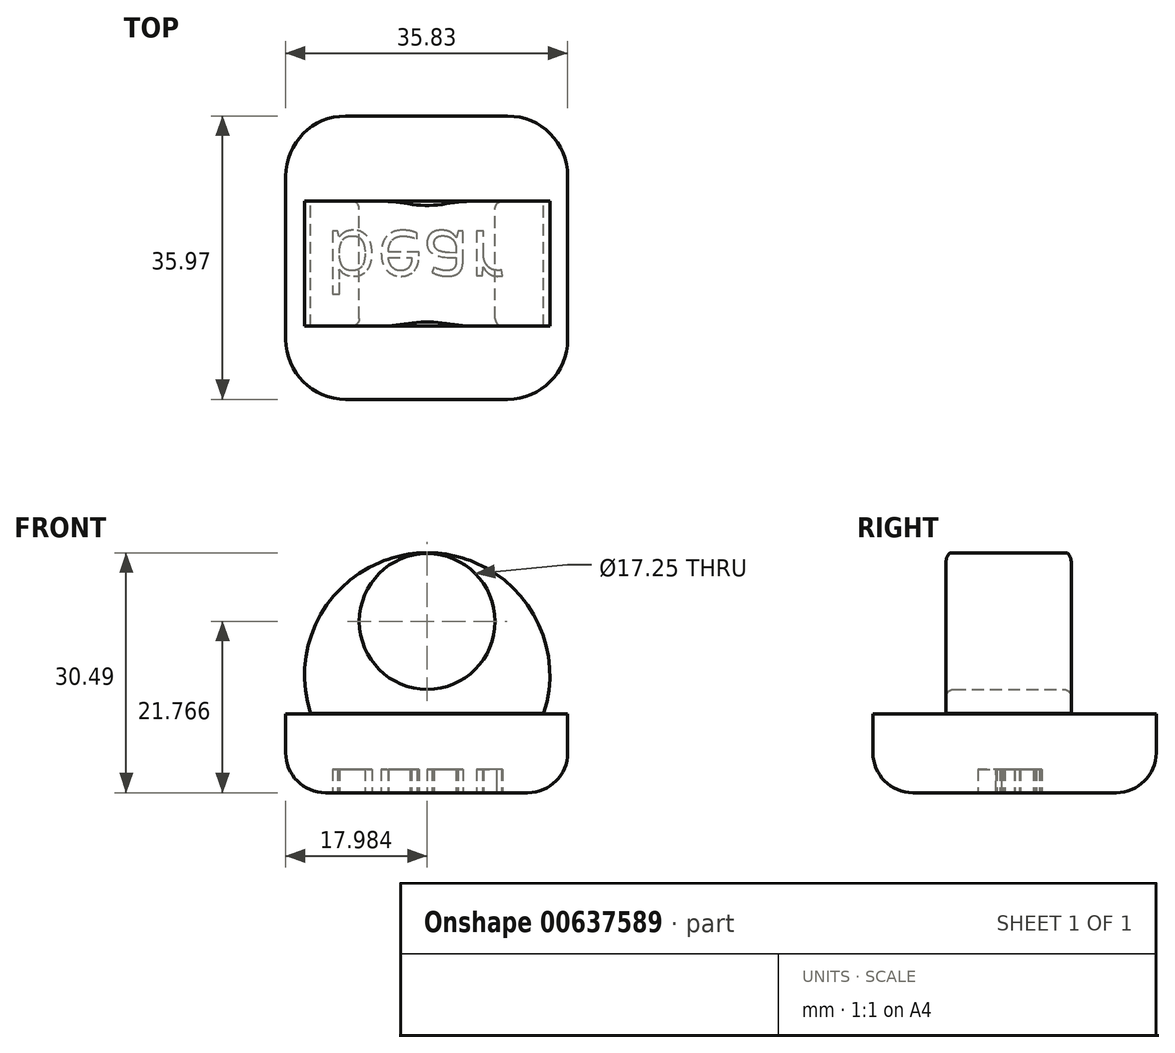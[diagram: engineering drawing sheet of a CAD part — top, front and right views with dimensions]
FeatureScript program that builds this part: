
annotation { "Feature Type Name" : "Feature", "Feature Type Description" : "" }
export const myFeature = defineFeature(function(context is Context, id is Id, definition is map)
    precondition{}
    {
        {
            var Q0;
            Q0=qCreatedBy(makeId("Top.planeOp"),FACE);
            var sketch = newSketch(context, id + "F0", { "sketchPlane" : qUnion([Q0])});
            skLineSegment(sketch, "E0", {"start": v(-35.83, -25.18) * mm, "end": v(0, -25.18) * mm});
            skLineSegment(sketch, "E1", {"start": v(0, -25.18) * mm, "end": v(0, 10.8) * mm});
            skLineSegment(sketch, "E2", {"start": v(0, 10.8) * mm, "end": v(-35.83, 10.8) * mm});
            skLineSegment(sketch, "E3", {"start": v(-35.83, 10.8) * mm, "end": v(-35.83, -25.18) * mm});
            skSolve(sketch);
        }
        {
            var Q0;
            Q0 = qSketchRegion(id + "F0", true);
            extrude(context, id + "F1", {"entities" : qUnion([Q0]), "depth" : 10 * mm, "offsetDistance" : 25.4 * mm});
        }
        {
            var Q0;
            Q0=qCreatedBy(makeId("Front.planeOp"),FACE);
            var sketch = newSketch(context, id + "F2", { "sketchPlane" : qUnion([Q0])});
            skLineSegment(sketch, "E4", {"start": v(-32.65, 10.06) * mm, "end": v(-29.6, 10.06) * mm});
            skLineSegment(sketch, "E5", {"start": v(-3.05, 10.06) * mm, "end": v(-6.1, 10.06) * mm});
            skPoint(sketch, "E6.orphan", {"position": v(-35.7, 10.06) * mm});
            skPoint(sketch, "E7.orphan", {"position": v(0, 10.06) * mm});
            skCircle(sketch, "E8", {"center": v(-17.85, 21.77) * mm, "radius": 8.63 * mm});
            skArc(sketch, "E9", {"start": v(-3.05, 10.06) * mm, "mid": v(-17.85, 30.5) * mm, "end": v(-32.65, 10.06) * mm});
            skLineSegment(sketch, "E10", {"start": v(-29.6, 10.06) * mm, "end": v(-6.1, 10.06) * mm});
            skSolve(sketch);
        }
        {
            var Q0;
            Q0=makeQuery(id+"F1.opExtrude","SWEPT_EDGE",EDGE,{"disambiguationData":[OSD([sQuery(id+"F0.wireOp",EDGE,"E0"),sQuery(id+"F0.wireOp",EDGE,"E3")])]});
            var Q1;
            Q1=makeQuery(id+"F1.opExtrude","SWEPT_EDGE",EDGE,{"disambiguationData":[OSD([sQuery(id+"F0.wireOp",EDGE,"E2"),sQuery(id+"F0.wireOp",EDGE,"E3")])]});
            var Q2;
            Q2=makeQuery(id+"F1.opExtrude","SWEPT_EDGE",EDGE,{"disambiguationData":[OSD([sQuery(id+"F0.wireOp",EDGE,"E1"),sQuery(id+"F0.wireOp",EDGE,"E2")])]});
            var Q3;
            Q3=makeQuery(id+"F1.opExtrude","SWEPT_EDGE",EDGE,{"disambiguationData":[OSD([sQuery(id+"F0.wireOp",EDGE,"E0"),sQuery(id+"F0.wireOp",EDGE,"E1")])]});
            fillet(context, id + "F3", {"entities" : qUnion([Q0, Q1, Q2, Q3]), "radius" : 7.62 * mm, "tangentPropagation" : true, "allowEdgeOverflow" : false});
        }
        {
            var Q0;
            Q0=makeQuery(id+"F1.opExtrude","CAP_EDGE",EDGE,{"disambiguationData":[OSD([sQuery(id+"F0.wireOp",EDGE,"E0")])],"isStart":true});
            var Q1;
            Q1=makeQuery(id+"F1.opExtrude","CAP_EDGE",EDGE,{"disambiguationData":[OSD([sQuery(id+"F0.wireOp",EDGE,"E3")])],"isStart":true});
            var Q2;
            {var subQ0=sQuery(id+"F0.wireOp",EDGE,"E3");var subQ1=sQuery(id+"F0.wireOp",EDGE,"E0");Q2=makeQuery(id+"F3.opFillet","BLEND_EDGE",EDGE,{"blendedFrom":[makeQuery(id+"F1.opExtrude","SWEPT_EDGE",EDGE,{"disambiguationData":[OSD([subQ1,subQ0])]}),makeQuery(id+"F1.opExtrude","CAP_FACE",FACE,{"disambiguationData":[OSD([subQ1,sQuery(id+"F0.wireOp",EDGE,"E1"),sQuery(id+"F0.wireOp",EDGE,"E2"),subQ0])],"isStart":true})],"blendedInto":[makeQuery(id+"F1.opExtrude","CAP_FACE",FACE,{"disambiguationData":[OSD([subQ1,sQuery(id+"F0.wireOp",EDGE,"E1"),sQuery(id+"F0.wireOp",EDGE,"E2"),subQ0])],"isStart":true})]});}
            var Q3;
            {var subQ0=sQuery(id+"F0.wireOp",EDGE,"E1");var subQ1=sQuery(id+"F0.wireOp",EDGE,"E0");Q3=makeQuery(id+"F3.opFillet","BLEND_EDGE",EDGE,{"blendedFrom":[makeQuery(id+"F1.opExtrude","SWEPT_EDGE",EDGE,{"disambiguationData":[OSD([subQ1,subQ0])]}),makeQuery(id+"F1.opExtrude","CAP_FACE",FACE,{"disambiguationData":[OSD([subQ1,subQ0,sQuery(id+"F0.wireOp",EDGE,"E2"),sQuery(id+"F0.wireOp",EDGE,"E3")])],"isStart":true})],"blendedInto":[makeQuery(id+"F1.opExtrude","CAP_FACE",FACE,{"disambiguationData":[OSD([subQ1,subQ0,sQuery(id+"F0.wireOp",EDGE,"E2"),sQuery(id+"F0.wireOp",EDGE,"E3")])],"isStart":true})]});}
            var Q4;
            Q4=makeQuery(id+"F1.opExtrude","CAP_EDGE",EDGE,{"disambiguationData":[OSD([sQuery(id+"F0.wireOp",EDGE,"E1")])],"isStart":true});
            var Q5;
            {var subQ0=sQuery(id+"F0.wireOp",EDGE,"E2");var subQ1=sQuery(id+"F0.wireOp",EDGE,"E1");Q5=makeQuery(id+"F3.opFillet","BLEND_EDGE",EDGE,{"blendedFrom":[makeQuery(id+"F1.opExtrude","SWEPT_EDGE",EDGE,{"disambiguationData":[OSD([subQ1,subQ0])]}),makeQuery(id+"F1.opExtrude","CAP_FACE",FACE,{"disambiguationData":[OSD([sQuery(id+"F0.wireOp",EDGE,"E0"),subQ1,subQ0,sQuery(id+"F0.wireOp",EDGE,"E3")])],"isStart":true})],"blendedInto":[makeQuery(id+"F1.opExtrude","CAP_FACE",FACE,{"disambiguationData":[OSD([sQuery(id+"F0.wireOp",EDGE,"E0"),subQ1,subQ0,sQuery(id+"F0.wireOp",EDGE,"E3")])],"isStart":true})]});}
            var Q6;
            Q6=makeQuery(id+"F1.opExtrude","CAP_EDGE",EDGE,{"disambiguationData":[OSD([sQuery(id+"F0.wireOp",EDGE,"E2")])],"isStart":true});
            var Q7;
            {var subQ0=sQuery(id+"F0.wireOp",EDGE,"E3");var subQ1=sQuery(id+"F0.wireOp",EDGE,"E2");Q7=makeQuery(id+"F3.opFillet","BLEND_EDGE",EDGE,{"blendedFrom":[makeQuery(id+"F1.opExtrude","SWEPT_EDGE",EDGE,{"disambiguationData":[OSD([subQ1,subQ0])]}),makeQuery(id+"F1.opExtrude","CAP_FACE",FACE,{"disambiguationData":[OSD([sQuery(id+"F0.wireOp",EDGE,"E0"),sQuery(id+"F0.wireOp",EDGE,"E1"),subQ1,subQ0])],"isStart":true})],"blendedInto":[makeQuery(id+"F1.opExtrude","CAP_FACE",FACE,{"disambiguationData":[OSD([sQuery(id+"F0.wireOp",EDGE,"E0"),sQuery(id+"F0.wireOp",EDGE,"E1"),subQ1,subQ0])],"isStart":true})]});}
            fillet(context, id + "F4", {"entities" : qUnion([Q0, Q1, Q2, Q3, Q4, Q5, Q6, Q7]), "radius" : 5.08 * mm, "tangentPropagation" : true, "allowEdgeOverflow" : false});
        }
        {
            var Q0;
            Q0=makeQuery(id+"F1.opExtrude","CAP_FACE",FACE,{"disambiguationData":[OSD([sQuery(id+"F0.wireOp",EDGE,"E0"),sQuery(id+"F0.wireOp",EDGE,"E1"),sQuery(id+"F0.wireOp",EDGE,"E2"),sQuery(id+"F0.wireOp",EDGE,"E3")])],"isStart":true});
            var sketch = newSketch(context, id + "F5", { "sketchPlane" : qUnion([Q0])});
            skText(sketch, "E11", { "text": "bear", "fontName": "OpenSans-Regular.ttf"});
            const initialGuessF5  = {"E11": [-0.03075, 0.0038, 1, 0, 0.00761]};
            skSetInitialGuess(sketch, initialGuessF5);
            skSolve(sketch);
        }
        {
            var Q0;
            Q0 = qSketchRegion(id + "F5", true);
            extrude(context, id + "F6", {"entities" : qUnion([Q0]), "operationType" : NewBodyOperationType.REMOVE, "oppositeDirection" : true, "depth" : 3 * mm, "offsetDistance" : 25 * mm});
        }
        {
            var Q0;
            Q0 = qSketchRegion(id + "F2", true);
            extrude(context, id + "F7", {"entities" : qUnion([Q0]), "depth" : 15.9 * mm, "offsetDistance" : 25 * mm});
        }
        {
            var Q0;
            Q0=makeQuery(id+"F7.opExtrude","CAP_EDGE",EDGE,{"disambiguationData":[OSD([sQuery(id+"F2.wireOp",EDGE,"E8")])],"isStart":true});
            var Q1;
            Q1=makeQuery(id+"F7.opExtrude","CAP_EDGE",EDGE,{"disambiguationData":[OSD([sQuery(id+"F2.wireOp",EDGE,"E8")])],"isStart":false});
            fillet(context, id + "F8", {"entities" : qUnion([Q0, Q1]), "radius" : 1 * mm, "tangentPropagation" : true, "allowEdgeOverflow" : false});
        }
    });
